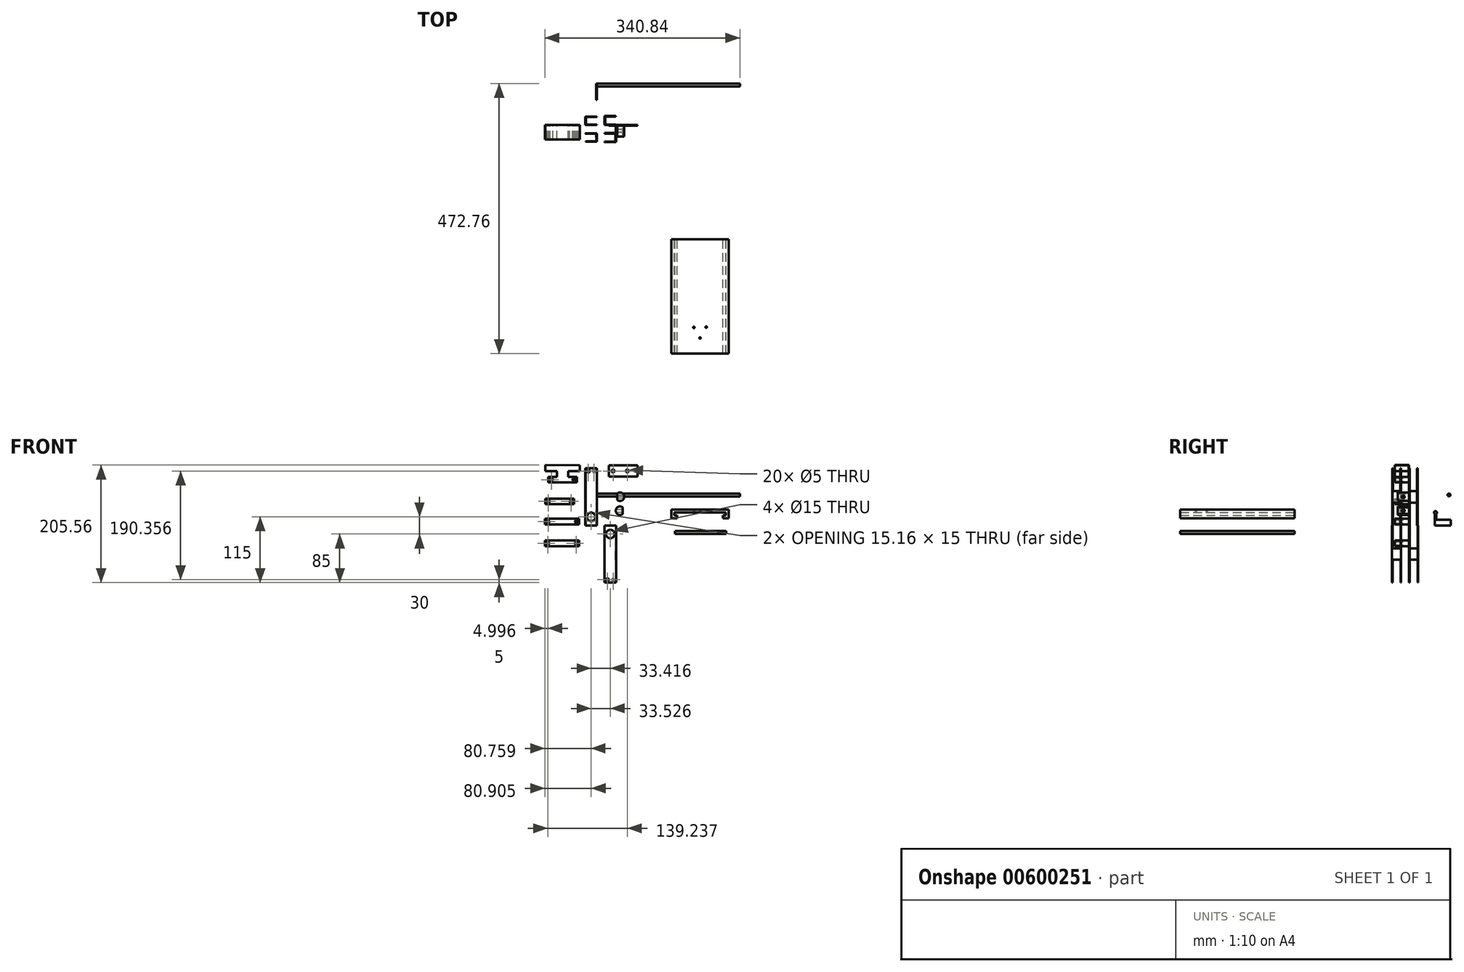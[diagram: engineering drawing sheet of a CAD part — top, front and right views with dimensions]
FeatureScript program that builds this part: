
annotation { "Feature Type Name" : "Feature", "Feature Type Description" : "" }
export const myFeature = defineFeature(function(context is Context, id is Id, definition is map)
    precondition{}
    {
        {
            var Q0;
            Q0=qCreatedBy(makeId("Top.planeOp"),FACE);
            var sketch = newSketch(context, id + "F0", { "sketchPlane" : qUnion([Q0])});
            skLineSegment(sketch, "E0", {"start": v(0, 15) * mm, "end": v(-20, 15) * mm});
            skLineSegment(sketch, "E1", {"start": v(-20, 15) * mm, "end": v(-20, 0) * mm});
            skLineSegment(sketch, "E2", {"start": v(-20, 0) * mm, "end": v(0, 0) * mm});
            skLineSegment(sketch, "E3", {"start": v(0, 0) * mm, "end": v(0, 1) * mm});
            skLineSegment(sketch, "E4", {"start": v(0, 1) * mm, "end": v(-19, 1) * mm});
            skLineSegment(sketch, "E5", {"start": v(-19, 1) * mm, "end": v(-19, 14) * mm});
            skLineSegment(sketch, "E6", {"start": v(-19, 14) * mm, "end": v(0, 14) * mm});
            skLineSegment(sketch, "E7", {"start": v(0, 14) * mm, "end": v(0, 15) * mm});
            skLineSegment(sketch, "E8", {"start": v(33.42, 1) * mm, "end": v(14.42, 1) * mm});
            skLineSegment(sketch, "E9", {"start": v(14.42, 1) * mm, "end": v(14.42, 15) * mm});
            skLineSegment(sketch, "E10", {"start": v(14.42, 15) * mm, "end": v(33.42, 15) * mm});
            skLineSegment(sketch, "E11", {"start": v(33.42, 15) * mm, "end": v(33.42, 16) * mm});
            skLineSegment(sketch, "E12", {"start": v(33.42, 16) * mm, "end": v(13.42, 16) * mm});
            skLineSegment(sketch, "E13", {"start": v(13.42, 16) * mm, "end": v(13.42, 0) * mm});
            skLineSegment(sketch, "E14", {"start": v(13.42, 0) * mm, "end": v(33.42, 0) * mm});
            skLineSegment(sketch, "E15", {"start": v(33.42, 0) * mm, "end": v(33.42, 1) * mm});
            skLineSegment(sketch, "E16", {"start": v(-36.62, -7.13) * mm, "end": v(38.64, -6.85) * mm, "construction": true});
            skLineSegment(sketch, "E17.MirrorCS", {"start": v(-19, 16) * mm, "end": v(0, 16) * mm});
            skLineSegment(sketch, "E18.MirrorCS", {"start": v(-19.95, -14.13) * mm, "end": v(0.05, -13.99) * mm});
            skLineSegment(sketch, "E19.MirrorCS", {"start": v(0.16, -28.99) * mm, "end": v(-19.84, -29.13) * mm});
            skLineSegment(sketch, "E20.MirrorCS", {"start": v(13.47, -13.89) * mm, "end": v(33.47, -13.74) * mm});
            skLineSegment(sketch, "E21.MirrorCS", {"start": v(33.58, -29.74) * mm, "end": v(13.58, -29.89) * mm});
            skLineSegment(sketch, "E22", {"start": v(13.47, -13.89) * mm, "end": v(13.47, -14.89) * mm});
            skLineSegment(sketch, "E23", {"start": v(13.47, -14.89) * mm, "end": v(32.47, -14.75) * mm});
            skLineSegment(sketch, "E24", {"start": v(32.58, -28.75) * mm, "end": v(13.58, -28.89) * mm});
            skLineSegment(sketch, "E25", {"start": v(13.58, -28.89) * mm, "end": v(13.58, -29.89) * mm});
            skLineSegment(sketch, "E26", {"start": v(32.58, -28.75) * mm, "end": v(32.47, -14.75) * mm});
            skLineSegment(sketch, "E27", {"start": v(33.47, -13.74) * mm, "end": v(33.58, -29.74) * mm});
            skLineSegment(sketch, "E28", {"start": v(0.05, -13.99) * mm, "end": v(0.16, -28.99) * mm});
            skLineSegment(sketch, "E29", {"start": v(-19.95, -14.13) * mm, "end": v(-19.94, -15.13) * mm});
            skLineSegment(sketch, "E30", {"start": v(-19.94, -15.13) * mm, "end": v(-0.94, -15) * mm});
            skLineSegment(sketch, "E31", {"start": v(-0.94, -15) * mm, "end": v(-0.85, -28) * mm});
            skLineSegment(sketch, "E32", {"start": v(-0.85, -28) * mm, "end": v(-19.84, -28.13) * mm});
            skLineSegment(sketch, "E33", {"start": v(-19.84, -29.13) * mm, "end": v(-19.84, -28.13) * mm});
            skSolve(sketch);
        }
        {
            var Q0;
            Q0=makeQuery(id+"F0.imprint","IMPRINT",FACE,{"disambiguationData":[TD([[makeQuery(id+"F0.imprint","IMPRINT",EDGE,{"derivedFrom":sQuery(id+"F0.wireOp",EDGE,"E0")}),1.0]])]});
            var Q1;
            Q1=makeQuery(id+"F0.imprint","IMPRINT",FACE,{"disambiguationData":[TD([[makeQuery(id+"F0.imprint","IMPRINT",EDGE,{"derivedFrom":sQuery(id+"F0.wireOp",EDGE,"E19.MirrorCS")}),-1.0]])]});
            extrude(context, id + "F1", {"entities" : qUnion([Q0, Q1]), "depth" : 100 * mm, "offsetDistance" : 25 * mm});
        }
        {
            var Q0;
            Q0=makeQuery(id+"F1.opExtrude","SWEPT_FACE",FACE,{"disambiguationData":[OSD([sQuery(id+"F0.wireOp",EDGE,"E2")])]});
            var sketch = newSketch(context, id + "F2", { "sketchPlane" : qUnion([Q0])});
            skCircle(sketch, "E34", {"center": v(-10, 15) * mm, "radius": 7.5 * mm});
            skPoint(sketch, "E34.centerSnap0", {"position": v(-10, 0) * mm});
            skCircle(sketch, "E35", {"center": v(-5, 95) * mm, "radius": 2.5 * mm});
            skSolve(sketch);
        }
        {
            var Q0;
            Q0=makeQuery(id+"F2.imprint","IMPRINT",FACE,{"disambiguationData":[TD([[makeQuery(id+"F2.imprint","IMPRINT",EDGE,{"derivedFrom":sQuery(id+"F2.wireOp",EDGE,"E34")}),1.0]])]});
            var Q1;
            Q1=makeQuery(id+"F2.imprint","IMPRINT",FACE,{"disambiguationData":[TD([[makeQuery(id+"F2.imprint","IMPRINT",EDGE,{"derivedFrom":sQuery(id+"F2.wireOp",EDGE,"E35")}),1.0]])]});
            extrude(context, id + "F3", {"entities" : qUnion([Q0, Q1]), "operationType" : NewBodyOperationType.REMOVE, "endBound" : BoundingType.THROUGH_ALL, "oppositeDirection" : true, "depth" : 25 * mm, "offsetDistance" : 25 * mm});
        }
        {
            var Q0;
            Q0=makeQuery(id+"F1.opExtrude","SWEPT_FACE",FACE,{"disambiguationData":[OSD([sQuery(id+"F0.wireOp",EDGE,"E1")])]});
            var sketch = newSketch(context, id + "F4", { "sketchPlane" : qUnion([Q0])});
            skPoint(sketch, "E36.centerSnap0", {"position": v(-7.5, 0) * mm});
            skLineSegment(sketch, "E37", {"start": v(-14, 0) * mm, "end": v(-14, 40) * mm});
            skLineSegment(sketch, "E38", {"start": v(-14, 40) * mm, "end": v(-1, 40) * mm});
            skLineSegment(sketch, "E39", {"start": v(-1, 40) * mm, "end": v(-1, 0) * mm});
            skLineSegment(sketch, "E40", {"start": v(-14, 100) * mm, "end": v(-14, 60) * mm});
            skLineSegment(sketch, "E41", {"start": v(-14, 60) * mm, "end": v(-1, 60) * mm});
            skLineSegment(sketch, "E42", {"start": v(-1, 60) * mm, "end": v(-1, 100) * mm});
            skSolve(sketch);
        }
        {
            var Q0;
            {var subQ0=sQuery(id+"F4.wireOp",EDGE,"E37");Q0=makeQuery(id+"F4.imprint","IMPRINT",FACE,{"disambiguationData":[TD([[makeQuery(id+"F4.imprint","IMPRINT",EDGE,{"derivedFrom":subQ0}),-1.0]])]});}
            var Q1;
            {var subQ0=sQuery(id+"F4.wireOp",EDGE,"E40");Q1=makeQuery(id+"F4.imprint","IMPRINT",FACE,{"disambiguationData":[TD([[makeQuery(id+"F4.imprint","IMPRINT",EDGE,{"derivedFrom":subQ0}),1.0]])]});}
            extrude(context, id + "F5", {"entities" : qUnion([Q0, Q1]), "operationType" : NewBodyOperationType.REMOVE, "endBound" : BoundingType.THROUGH_ALL, "oppositeDirection" : true, "depth" : 25 * mm, "offsetDistance" : 25 * mm});
        }
        {
            var Q0;
            Q0=makeQuery(id+"F0.imprint","IMPRINT",FACE,{"disambiguationData":[TD([[makeQuery(id+"F0.imprint","IMPRINT",EDGE,{"derivedFrom":sQuery(id+"F0.wireOp",EDGE,"E8")}),1.0]])]});
            var Q1;
            Q1=makeQuery(id+"F0.imprint","IMPRINT",FACE,{"disambiguationData":[TD([[makeQuery(id+"F0.imprint","IMPRINT",EDGE,{"derivedFrom":sQuery(id+"F0.wireOp",EDGE,"E20.MirrorCS")}),-1.0]])]});
            extrude(context, id + "F6", {"entities" : qUnion([Q0, Q1]), "oppositeDirection" : true, "depth" : 100 * mm, "offsetDistance" : 25 * mm});
        }
        {
            var Q0;
            Q0=makeQuery(id+"F6.opExtrude","SWEPT_FACE",FACE,{"disambiguationData":[OSD([sQuery(id+"F0.wireOp",EDGE,"E14")])]});
            var sketch = newSketch(context, id + "F7", { "sketchPlane" : qUnion([Q0])});
            skCircle(sketch, "E43", {"center": v(23.42, -15) * mm, "radius": 7.5 * mm});
            skPoint(sketch, "E43.centerSnap0", {"position": v(23.42, 0) * mm});
            skCircle(sketch, "E44", {"center": v(28.42, -95) * mm, "radius": 2.5 * mm});
            skSolve(sketch);
        }
        {
            var Q0;
            Q0=makeQuery(id+"F7.imprint","IMPRINT",FACE,{"disambiguationData":[TD([[makeQuery(id+"F7.imprint","IMPRINT",EDGE,{"derivedFrom":sQuery(id+"F7.wireOp",EDGE,"E43")}),1.0]])]});
            var Q1;
            Q1=makeQuery(id+"F7.imprint","IMPRINT",FACE,{"disambiguationData":[TD([[makeQuery(id+"F7.imprint","IMPRINT",EDGE,{"derivedFrom":sQuery(id+"F7.wireOp",EDGE,"E44")}),1.0]])]});
            extrude(context, id + "F8", {"entities" : qUnion([Q0, Q1]), "operationType" : NewBodyOperationType.REMOVE, "endBound" : BoundingType.THROUGH_ALL, "oppositeDirection" : true, "depth" : 25 * mm, "offsetDistance" : 25 * mm});
        }
        {
            var Q0;
            Q0=makeQuery(id+"F6.opExtrude","SWEPT_FACE",FACE,{"disambiguationData":[OSD([sQuery(id+"F0.wireOp",EDGE,"E13")])]});
            var sketch = newSketch(context, id + "F9", { "sketchPlane" : qUnion([Q0])});
            skLineSegment(sketch, "E45", {"start": v(-15, 0) * mm, "end": v(-15, -40) * mm});
            skLineSegment(sketch, "E46", {"start": v(-15, -40) * mm, "end": v(-1, -40) * mm});
            skLineSegment(sketch, "E47", {"start": v(-1, -40) * mm, "end": v(-1, 0) * mm});
            skLineSegment(sketch, "E48", {"start": v(-15, -100) * mm, "end": v(-15, -60) * mm});
            skLineSegment(sketch, "E49", {"start": v(-15, -60) * mm, "end": v(-1, -60) * mm});
            skLineSegment(sketch, "E50", {"start": v(-1, -60) * mm, "end": v(-1, -100) * mm});
            skSolve(sketch);
        }
        {
            var Q0;
            {var subQ0=sQuery(id+"F9.wireOp",EDGE,"E45");Q0=makeQuery(id+"F9.imprint","IMPRINT",FACE,{"disambiguationData":[TD([[makeQuery(id+"F9.imprint","IMPRINT",EDGE,{"derivedFrom":subQ0}),1.0]])]});}
            var Q1;
            {var subQ0=sQuery(id+"F9.wireOp",EDGE,"E48");Q1=makeQuery(id+"F9.imprint","IMPRINT",FACE,{"disambiguationData":[TD([[makeQuery(id+"F9.imprint","IMPRINT",EDGE,{"derivedFrom":subQ0}),-1.0]])]});}
            extrude(context, id + "F10", {"entities" : qUnion([Q0, Q1]), "operationType" : NewBodyOperationType.REMOVE, "endBound" : BoundingType.THROUGH_ALL, "oppositeDirection" : true, "depth" : 25 * mm, "offsetDistance" : 25 * mm});
        }
        {
            var Q0;
            Q0=qCreatedBy(makeId("Front.planeOp"),FACE);
            var sketch = newSketch(context, id + "F11", { "sketchPlane" : qUnion([Q0])});
            skLineSegment(sketch, "E51.bottom", {"start": v(20.9, 105.36) * mm, "end": v(70.9, 105.36) * mm});
            skLineSegment(sketch, "E51.top", {"start": v(20.9, 85.36) * mm, "end": v(70.9, 85.36) * mm});
            skLineSegment(sketch, "E51.left", {"start": v(20.9, 105.36) * mm, "end": v(20.9, 85.36) * mm});
            skLineSegment(sketch, "E51.right", {"start": v(70.9, 105.36) * mm, "end": v(70.9, 85.36) * mm});
            skCircle(sketch, "E52", {"center": v(28.4, 95.36) * mm, "radius": 2.5 * mm});
            skPoint(sketch, "E52.centerSnap0", {"position": v(20.9, 95.36) * mm});
            skCircle(sketch, "E53.MirrorC", {"center": v(53.4, 95.36) * mm, "radius": 2.5 * mm});
            skSolve(sketch);
        }
        {
            var Q0;
            Q0=makeQuery(id+"F11.imprint","IMPRINT",FACE,{"disambiguationData":[TD([[makeQuery(id+"F11.imprint","IMPRINT",EDGE,{"derivedFrom":sQuery(id+"F11.wireOp",EDGE,"E51.bottom")}),-1.0]])]});
            extrude(context, id + "F12", {"entities" : qUnion([Q0]), "depth" : 1 * mm, "offsetDistance" : 25 * mm});
        }
        {
            var Q0;
            Q0=makeQuery(id+"F1.opExtrude","SWEPT_FACE",FACE,{"disambiguationData":[OSD([sQuery(id+"F0.wireOp",EDGE,"E19.MirrorCS")])]});
            var sketch = newSketch(context, id + "F13", { "sketchPlane" : qUnion([Q0])});
            skCircle(sketch, "E54", {"center": v(-15.05, 95) * mm, "radius": 2.5 * mm});
            skCircle(sketch, "E55", {"center": v(-10.05, 15) * mm, "radius": 7.5 * mm});
            skPoint(sketch, "E55.centerSnap0", {"position": v(-10.05, 0) * mm});
            skSolve(sketch);
        }
        {
            var Q0;
            Q0=makeQuery(id+"F13.imprint","IMPRINT",FACE,{"disambiguationData":[TD([[makeQuery(id+"F13.imprint","IMPRINT",EDGE,{"derivedFrom":sQuery(id+"F13.wireOp",EDGE,"E54")}),1.0]])]});
            var Q1;
            Q1=makeQuery(id+"F13.imprint","IMPRINT",FACE,{"disambiguationData":[TD([[makeQuery(id+"F13.imprint","IMPRINT",EDGE,{"derivedFrom":sQuery(id+"F13.wireOp",EDGE,"E55")}),1.0]])]});
            extrude(context, id + "F14", {"entities" : qUnion([Q0, Q1]), "operationType" : NewBodyOperationType.REMOVE, "endBound" : BoundingType.THROUGH_ALL, "oppositeDirection" : true, "depth" : 25 * mm, "offsetDistance" : 25 * mm});
        }
        {
            var Q0;
            Q0=makeQuery(id+"F6.opExtrude","SWEPT_FACE",FACE,{"disambiguationData":[OSD([sQuery(id+"F0.wireOp",EDGE,"E21.MirrorCS")])]});
            var sketch = newSketch(context, id + "F15", { "sketchPlane" : qUnion([Q0])});
            skCircle(sketch, "E56", {"center": v(23.36, -15) * mm, "radius": 7.5 * mm});
            skPoint(sketch, "E56.centerSnap0", {"position": v(23.36, 0) * mm});
            skCircle(sketch, "E57", {"center": v(18.36, -95) * mm, "radius": 2.5 * mm});
            skSolve(sketch);
        }
        {
            var Q0;
            Q0=qSketchRegion(id+"F15",true);
            extrude(context, id + "F16", {"entities" : qUnion([Q0]), "operationType" : NewBodyOperationType.REMOVE, "endBound" : BoundingType.THROUGH_ALL, "oppositeDirection" : true, "depth" : 25 * mm, "offsetDistance" : 25 * mm});
        }
        {
            var Q0;
            Q0=makeQuery(id+"F6.opExtrude","SWEPT_FACE",FACE,{"disambiguationData":[OSD([sQuery(id+"F0.wireOp",EDGE,"E27")])]});
            var sketch = newSketch(context, id + "F17", { "sketchPlane" : qUnion([Q0])});
            skLineSegment(sketch, "E58", {"start": v(-14.99, -40) * mm, "end": v(-28.99, -40) * mm});
            skLineSegment(sketch, "E59", {"start": v(-28.99, -40) * mm, "end": v(-28.99, 0) * mm});
            skLineSegment(sketch, "E60", {"start": v(-14.99, -40) * mm, "end": v(-14.99, 0) * mm});
            skLineSegment(sketch, "E61", {"start": v(-28.99, -100) * mm, "end": v(-28.99, -60) * mm});
            skLineSegment(sketch, "E62", {"start": v(-28.99, -60) * mm, "end": v(-14.99, -60) * mm});
            skLineSegment(sketch, "E63", {"start": v(-14.99, -60) * mm, "end": v(-14.99, -100) * mm});
            skSolve(sketch);
        }
        {
            var Q0;
            Q0=makeQuery(id+"F17.imprint","IMPRINT",FACE,{"disambiguationData":[TD([[makeQuery(id+"F17.imprint","IMPRINT",EDGE,{"derivedFrom":sQuery(id+"F17.wireOp",EDGE,"E58")}),-1.0]])]});
            var Q1;
            {var subQ0=sQuery(id+"F17.wireOp",EDGE,"E61");Q1=makeQuery(id+"F17.imprint","IMPRINT",FACE,{"disambiguationData":[TD([[makeQuery(id+"F17.imprint","IMPRINT",EDGE,{"derivedFrom":subQ0}),-1.0]])]});}
            extrude(context, id + "F18", {"entities" : qUnion([Q0, Q1]), "operationType" : NewBodyOperationType.REMOVE, "endBound" : BoundingType.THROUGH_ALL, "oppositeDirection" : true, "depth" : 25 * mm, "offsetDistance" : 25 * mm});
        }
        {
            var Q0;
            Q0=makeQuery(id+"F1.opExtrude","SWEPT_FACE",FACE,{"disambiguationData":[OSD([sQuery(id+"F0.wireOp",EDGE,"E28")])]});
            var sketch = newSketch(context, id + "F19", { "sketchPlane" : qUnion([Q0])});
            skLineSegment(sketch, "E64", {"start": v(-14.99, 0) * mm, "end": v(-14.99, 40) * mm});
            skLineSegment(sketch, "E65", {"start": v(-14.99, 40) * mm, "end": v(-27.99, 40) * mm});
            skLineSegment(sketch, "E66", {"start": v(-27.99, 40) * mm, "end": v(-27.99, 0) * mm});
            skLineSegment(sketch, "E67", {"start": v(-27.99, 100) * mm, "end": v(-27.99, 60) * mm});
            skLineSegment(sketch, "E68", {"start": v(-27.99, 60) * mm, "end": v(-14.99, 60) * mm});
            skLineSegment(sketch, "E69", {"start": v(-14.99, 60) * mm, "end": v(-14.99, 100) * mm});
            skSolve(sketch);
        }
        {
            var Q0;
            {var subQ0=sQuery(id+"F19.wireOp",EDGE,"E64");Q0=makeQuery(id+"F19.imprint","IMPRINT",FACE,{"disambiguationData":[TD([[makeQuery(id+"F19.imprint","IMPRINT",EDGE,{"derivedFrom":subQ0}),1.0]])]});}
            var Q1;
            {var subQ0=sQuery(id+"F19.wireOp",EDGE,"E67");Q1=makeQuery(id+"F19.imprint","IMPRINT",FACE,{"disambiguationData":[TD([[makeQuery(id+"F19.imprint","IMPRINT",EDGE,{"derivedFrom":subQ0}),1.0]])]});}
            extrude(context, id + "F20", {"entities" : qUnion([Q0, Q1]), "operationType" : NewBodyOperationType.REMOVE, "oppositeDirection" : true, "depth" : 25 * mm, "offsetDistance" : 25 * mm});
        }
        {
            var Q0;
            Q0=qCreatedBy(makeId("Front.planeOp"),FACE);
            var sketch = newSketch(context, id + "F21", { "sketchPlane" : qUnion([Q0])});
            skArc(sketch, "E70", {"start": v(35.49, 44.6) * mm, "mid": v(47.93, 50.24) * mm, "end": v(35.49, 55.88) * mm});
            skArc(sketch, "E71", {"start": v(45.38, 31.4) * mm, "mid": v(32.93, 25.77) * mm, "end": v(45.38, 20.13) * mm});
            skLineSegment(sketch, "E72", {"start": v(35.49, 55.88) * mm, "end": v(35.49, 44.6) * mm});
            skLineSegment(sketch, "E73.trimOffspring", {"start": v(45.38, 31.4) * mm, "end": v(45.38, 20.13) * mm});
            skPoint(sketch, "E74.orphan", {"position": v(40.43, 57.74) * mm});
            skSolve(sketch);
        }
        {
            var Q0;
            Q0=makeQuery(id+"F21.imprint","IMPRINT",FACE,{"disambiguationData":[TD([[makeQuery(id+"F21.imprint","IMPRINT",EDGE,{"derivedFrom":sQuery(id+"F21.wireOp",EDGE,"E70")}),1.0]])]});
            var Q1;
            Q1=makeQuery(id+"F21.imprint","IMPRINT",FACE,{"disambiguationData":[TD([[makeQuery(id+"F21.imprint","IMPRINT",EDGE,{"derivedFrom":sQuery(id+"F21.wireOp",EDGE,"E71")}),1.0]])]});
            extrude(context, id + "F22", {"entities" : qUnion([Q0, Q1]), "depth" : 20 * mm, "offsetDistance" : 25 * mm});
        }
        {
            var Q0;
            Q0=qCreatedBy(makeId("Right.planeOp"),FACE);
            var sketch = newSketch(context, id + "F23", { "sketchPlane" : qUnion([Q0])});
            skCircle(sketch, "E75", {"center": v(69.88, 53.43) * mm, "radius": 2.5 * mm});
            skSolve(sketch);
        }
        {
            var Q0;
            Q0=makeQuery(id+"F23.imprint","IMPRINT",FACE,{"disambiguationData":[TD([[makeQuery(id+"F23.imprint","IMPRINT",EDGE,{"derivedFrom":sQuery(id+"F23.wireOp",EDGE,"E75")}),1.0]])]});
            extrude(context, id + "F24", {"entities" : qUnion([Q0]), "depth" : 250 * mm, "offsetDistance" : 25 * mm});
        }
        {
            var Q0;
            Q0=qCreatedBy(makeId("Front.planeOp"),FACE);
            var sketch = newSketch(context, id + "F25", { "sketchPlane" : qUnion([Q0])});
            skLineSegment(sketch, "E76.top", {"start": v(-84.95, 75.12) * mm, "end": v(-34.95, 75.12) * mm});
            skLineSegment(sketch, "E76.left", {"start": v(-84.95, 85.12) * mm, "end": v(-84.95, 75.12) * mm});
            skLineSegment(sketch, "E76.right", {"start": v(-34.95, 85.12) * mm, "end": v(-34.95, 75.12) * mm});
            skCircle(sketch, "E77", {"center": v(-79.38, 80.12) * mm, "radius": 2.5 * mm});
            skPoint(sketch, "E77.centerSnap0", {"position": v(-84.95, 80.12) * mm});
            skCircle(sketch, "E78", {"center": v(-39.95, 80.12) * mm, "radius": 2.41 * mm});
            skPoint(sketch, "E78.centerSnap0", {"position": v(-34.95, 80.12) * mm});
            skLineSegment(sketch, "E79.MirrorCS", {"start": v(-89.95, 47.06) * mm, "end": v(-39.95, 47.06) * mm});
            skLineSegment(sketch, "E80.MirrorCS", {"start": v(-89.95, 37.06) * mm, "end": v(-89.95, 47.06) * mm});
            skLineSegment(sketch, "E81.MirrorCS", {"start": v(-89.95, 37.06) * mm, "end": v(-39.95, 37.06) * mm});
            skLineSegment(sketch, "E82.MirrorCS", {"start": v(-39.95, 37.06) * mm, "end": v(-39.95, 47.06) * mm});
            skCircle(sketch, "E83", {"center": v(-84.95, 42.06) * mm, "radius": 2.5 * mm});
            skPoint(sketch, "E83.centerSnap0", {"position": v(-89.95, 42.06) * mm});
            skCircle(sketch, "E84", {"center": v(-44.95, 42.06) * mm, "radius": 2.5 * mm});
            skPoint(sketch, "E84.centerSnap0", {"position": v(-39.95, 42.06) * mm});
            skLineSegment(sketch, "E85.bottom", {"start": v(-90.84, 11.74) * mm, "end": v(-30.84, 11.74) * mm});
            skLineSegment(sketch, "E85.top", {"start": v(-90.84, 1.74) * mm, "end": v(-30.84, 1.74) * mm});
            skLineSegment(sketch, "E85.left", {"start": v(-90.84, 11.74) * mm, "end": v(-90.84, 1.74) * mm});
            skLineSegment(sketch, "E85.right", {"start": v(-30.84, 11.74) * mm, "end": v(-30.84, 1.74) * mm});
            skCircle(sketch, "E86", {"center": v(-85.27, 6.74) * mm, "radius": 2.5 * mm});
            skPoint(sketch, "E86.centerSnap0", {"position": v(-90.84, 6.74) * mm});
            skCircle(sketch, "E87", {"center": v(-35.84, 6.74) * mm, "radius": 2.41 * mm});
            skPoint(sketch, "E87.centerSnap0", {"position": v(-30.84, 6.74) * mm});
            skLineSegment(sketch, "E88.MirrorCS", {"start": v(-90.84, -36.32) * mm, "end": v(-90.84, -26.32) * mm});
            skLineSegment(sketch, "E89.MirrorCS", {"start": v(-30.84, -36.32) * mm, "end": v(-30.84, -26.32) * mm});
            skCircle(sketch, "E90", {"center": v(-85.84, -31.32) * mm, "radius": 2.5 * mm});
            skPoint(sketch, "E90.centerSnap0", {"position": v(-90.84, -31.32) * mm});
            skCircle(sketch, "E91", {"center": v(-35.84, -31.32) * mm, "radius": 2.5 * mm});
            skPoint(sketch, "E91.centerSnap0", {"position": v(-30.84, -31.32) * mm});
            skLineSegment(sketch, "E92", {"start": v(-90.84, -26.32) * mm, "end": v(-30.84, -26.32) * mm});
            skLineSegment(sketch, "E93", {"start": v(-90.84, -36.32) * mm, "end": v(-30.84, -36.32) * mm});
            skLineSegment(sketch, "E94", {"start": v(-69.95, 85.12) * mm, "end": v(-69.95, 95.12) * mm});
            skLineSegment(sketch, "E95.MirrorCS", {"start": v(-49.95, 85.12) * mm, "end": v(-49.95, 95.12) * mm});
            skLineSegment(sketch, "E96.MirrorCS", {"start": v(-89.95, 135.12) * mm, "end": v(-39.95, 135.12) * mm});
            skLineSegment(sketch, "E97.MirrorCS", {"start": v(-84.95, 85.12) * mm, "end": v(-69.95, 85.12) * mm});
            skLineSegment(sketch, "E98", {"start": v(-89.95, 95.12) * mm, "end": v(-89.95, 105.56) * mm});
            skLineSegment(sketch, "E99", {"start": v(-29.95, 105.12) * mm, "end": v(-29.95, 95.12) * mm});
            skLineSegment(sketch, "E100.trimOffspring", {"start": v(-49.95, 95.12) * mm, "end": v(-29.95, 95.12) * mm});
            skLineSegment(sketch, "E101", {"start": v(-69.95, 95.12) * mm, "end": v(-89.95, 95.12) * mm});
            skLineSegment(sketch, "E102.trimOffspring", {"start": v(-49.95, 85.12) * mm, "end": v(-34.95, 85.12) * mm});
            skPoint(sketch, "E103.end.orphan", {"position": v(-59.95, 75.12) * mm});
            skPoint(sketch, "E103.start.orphan", {"position": v(-59.95, 85.12) * mm});
            skLineSegment(sketch, "E104", {"start": v(-29.95, 105.12) * mm, "end": v(-89.95, 105.56) * mm});
            skLineSegment(sketch, "E105", {"start": v(-59.95, 75.12) * mm, "end": v(-59.95, 105.34) * mm, "construction": true});
            skSolve(sketch);
        }
        {
            var Q0;
            Q0=makeQuery(id+"F25.imprint","IMPRINT",FACE,{"disambiguationData":[TD([[makeQuery(id+"F25.imprint","IMPRINT",EDGE,{"derivedFrom":sQuery(id+"F25.wireOp",EDGE,"E76.bottom")}),-1.0]])]});
            var Q1;
            {var subQ2=sQuery(id+"F25.wireOp",EDGE,"E80.MirrorCS");Q1=makeQuery(id+"F25.imprint","IMPRINT",FACE,{"disambiguationData":[TD([[makeQuery(id+"F25.imprint","IMPRINT",EDGE,{"derivedFrom":subQ2}),-1.0]])]});}
            var Q2;
            Q2=makeQuery(id+"F25.imprint","IMPRINT",FACE,{"disambiguationData":[TD([[makeQuery(id+"F25.imprint","IMPRINT",EDGE,{"derivedFrom":sQuery(id+"F25.wireOp",EDGE,"E76.top")}),1.0]])]});
            extrude(context, id + "F26", {"entities" : qUnion([Q0, Q1, Q2]), "depth" : 25 * mm, "offsetDistance" : 25 * mm});
        }
        {
            var Q0;
            Q0=makeQuery(id+"F25.imprint","IMPRINT",FACE,{"disambiguationData":[TD([[makeQuery(id+"F25.imprint","IMPRINT",EDGE,{"derivedFrom":sQuery(id+"F25.wireOp",EDGE,"E88.MirrorCS")}),-1.0]])]});
            var Q1;
            Q1=makeQuery(id+"F25.imprint","IMPRINT",FACE,{"disambiguationData":[TD([[makeQuery(id+"F25.imprint","IMPRINT",EDGE,{"derivedFrom":sQuery(id+"F25.wireOp",EDGE,"E85.bottom")}),-1.0]])]});
            extrude(context, id + "F27", {"entities" : qUnion([Q0, Q1]), "depth" : 25 * mm, "offsetDistance" : 25 * mm});
        }
        {
            var Q0;
            Q0=makeQuery(id+"F22.opExtrude","SWEPT_FACE",FACE,{"disambiguationData":[OSD([sQuery(id+"F21.wireOp",EDGE,"E73.trimOffspring")])]});
            var sketch = newSketch(context, id + "F28", { "sketchPlane" : qUnion([Q0])});
            skCircle(sketch, "E106", {"center": v(-10, 25.77) * mm, "radius": 2.5 * mm});
            skPoint(sketch, "E106.centerSnap0", {"position": v(-20, 25.77) * mm});
            skPoint(sketch, "E106.centerSnap1", {"position": v(-10, 31.4) * mm});
            skSolve(sketch);
        }
        {
            var Q0;
            Q0=makeQuery(id+"F28.imprint","IMPRINT",FACE,{"disambiguationData":[TD([[makeQuery(id+"F28.imprint","IMPRINT",EDGE,{"derivedFrom":sQuery(id+"F28.wireOp",EDGE,"E106")}),1.0]])]});
            extrude(context, id + "F29", {"entities" : qUnion([Q0]), "operationType" : NewBodyOperationType.REMOVE, "endBound" : BoundingType.THROUGH_ALL, "oppositeDirection" : true, "depth" : 25 * mm, "offsetDistance" : 25 * mm});
        }
        {
            var Q0;
            Q0=makeQuery(id+"F22.opExtrude","SWEPT_FACE",FACE,{"disambiguationData":[OSD([sQuery(id+"F21.wireOp",EDGE,"E72")])]});
            var sketch = newSketch(context, id + "F30", { "sketchPlane" : qUnion([Q0])});
            skCircle(sketch, "E107", {"center": v(10, 50.24) * mm, "radius": 2.5 * mm});
            skPoint(sketch, "E107.centerSnap0", {"position": v(10, 44.6) * mm});
            skPoint(sketch, "E107.centerSnap1", {"position": v(0, 50.24) * mm});
            skSolve(sketch);
        }
        {
            var Q0;
            Q0=makeQuery(id+"F30.imprint","IMPRINT",FACE,{"disambiguationData":[TD([[makeQuery(id+"F30.imprint","IMPRINT",EDGE,{"derivedFrom":sQuery(id+"F30.wireOp",EDGE,"E107")}),1.0]])]});
            extrude(context, id + "F31", {"entities" : qUnion([Q0]), "operationType" : NewBodyOperationType.REMOVE, "endBound" : BoundingType.THROUGH_ALL, "oppositeDirection" : true, "depth" : 25 * mm, "offsetDistance" : 25 * mm});
        }
        {
            var Q0;
            Q0=qCreatedBy(makeId("Right.planeOp"),FACE);
            var sketch = newSketch(context, id + "F32", { "sketchPlane" : qUnion([Q0])});
            skArc(sketch, "E108", {"start": v(47.76, 20.47) * mm, "mid": v(46.3, 25) * mm, "end": v(44.85, 20.47) * mm});
            skLineSegment(sketch, "E109", {"start": v(47.76, 8.68) * mm, "end": v(47.76, 20.47) * mm});
            skLineSegment(sketch, "E110.MirrorCS", {"start": v(44.85, 8.68) * mm, "end": v(44.85, 20.47) * mm});
            skLineSegment(sketch, "E111", {"start": v(37.92, 27.31) * mm, "end": v(57.96, 27.31) * mm, "construction": true});
            skLineSegment(sketch, "E112", {"start": v(44.85, 8.68) * mm, "end": v(44.85, 0) * mm});
            skLineSegment(sketch, "E113", {"start": v(44.85, 0) * mm, "end": v(47.76, 0) * mm});
            skLineSegment(sketch, "E114", {"start": v(47.76, 0) * mm, "end": v(47.76, 8.68) * mm});
            skArc(sketch, "E115.MirrorCS", {"start": v(47.76, 34.16) * mm, "mid": v(46.3, 29.63) * mm, "end": v(44.85, 34.16) * mm});
            skLineSegment(sketch, "E116.MirrorCS", {"start": v(44.85, 45.94) * mm, "end": v(44.85, 34.16) * mm});
            skLineSegment(sketch, "E117.MirrorCS", {"start": v(47.76, 45.94) * mm, "end": v(47.76, 34.16) * mm});
            skLineSegment(sketch, "E118.MirrorCS", {"start": v(44.85, 45.94) * mm, "end": v(44.85, 54.62) * mm});
            skLineSegment(sketch, "E119.MirrorCS", {"start": v(47.76, 54.62) * mm, "end": v(47.76, 45.94) * mm});
            skLineSegment(sketch, "E120.MirrorCS", {"start": v(44.85, 54.62) * mm, "end": v(47.76, 54.62) * mm});
            skSolve(sketch);
        }
        {
            var Q0;
            Q0=makeQuery(id+"F32.imprint","IMPRINT",FACE,{"disambiguationData":[TD([[makeQuery(id+"F32.imprint","IMPRINT",EDGE,{"derivedFrom":sQuery(id+"F32.wireOp",EDGE,"E108")}),1.0]])]});
            var Q1;
            Q1=makeQuery(id+"F32.imprint","IMPRINT",FACE,{"disambiguationData":[TD([[makeQuery(id+"F32.imprint","IMPRINT",EDGE,{"derivedFrom":sQuery(id+"F32.wireOp",EDGE,"E115.MirrorCS")}),-1.0]])]});
            extrude(context, id + "F33", {"entities" : qUnion([Q0, Q1]), "oppositeDirection" : true, "depth" : 1 * mm, "offsetDistance" : 25 * mm});
        }
        {
            var Q0;
            Q0=makeQuery(id+"F33.opExtrude","SWEPT_FACE",FACE,{"disambiguationData":[OSD([sQuery(id+"F32.wireOp",EDGE,"E109"),sQuery(id+"F32.wireOp",EDGE,"E114")])]});
            var sketch = newSketch(context, id + "F34", { "sketchPlane" : qUnion([Q0])});
            skLineSegment(sketch, "E121", {"start": v(0, 10) * mm, "end": v(1, 10) * mm});
            skLineSegment(sketch, "E122", {"start": v(0.98, 44.62) * mm, "end": v(0, 44.62) * mm});
            skSolve(sketch);
        }
        {
            var Q0;
            {var subQ0=sQuery(id+"F34.wireOp",EDGE,"E121");Q0=makeQuery(id+"F34.imprint","IMPRINT",FACE,{"disambiguationData":[TD([[makeQuery(id+"F34.imprint","IMPRINT",EDGE,{"derivedFrom":subQ0}),-1.0]])]});}
            extrude(context, id + "F35", {"entities" : qUnion([Q0]), "operationType" : NewBodyOperationType.ADD, "depth" : 25 * mm, "offsetDistance" : 25 * mm});
        }
        {
            var Q0;
            Q0=qCreatedBy(makeId("Front.planeOp"),FACE);
            var sketch = newSketch(context, id + "F36", { "sketchPlane" : qUnion([Q0])});
            skLineSegment(sketch, "E123", {"start": v(181.33, -15) * mm, "end": v(136.33, -15) * mm});
            skLineSegment(sketch, "E124", {"start": v(136.33, -15) * mm, "end": v(136.33, -10) * mm});
            skLineSegment(sketch, "E125", {"start": v(136.33, -10) * mm, "end": v(181.33, -10) * mm});
            skLineSegment(sketch, "E126", {"start": v(181.33, -10) * mm, "end": v(181.33, -15) * mm, "construction": true});
            skLineSegment(sketch, "E127.MirrorCS", {"start": v(226.33, -10) * mm, "end": v(181.33, -10) * mm});
            skLineSegment(sketch, "E128.MirrorCS", {"start": v(181.33, -15) * mm, "end": v(226.33, -15) * mm});
            skLineSegment(sketch, "E129.MirrorCS", {"start": v(226.33, -15) * mm, "end": v(226.33, -10) * mm});
            skLineSegment(sketch, "E130", {"start": v(119.38, 8.74) * mm, "end": v(249.77, 8.74) * mm, "construction": true});
            skLineSegment(sketch, "E131.MirrorCS", {"start": v(243.3, 8.74) * mm, "end": v(112.9, 8.74) * mm, "construction": true});
            skLineSegment(sketch, "E132.MirrorCS", {"start": v(180.38, 22.49) * mm, "end": v(180.38, 27.49) * mm, "construction": true});
            skLineSegment(sketch, "E133.MirrorCS", {"start": v(220.38, 12.49) * mm, "end": v(220.38, 17.49) * mm});
            skLineSegment(sketch, "E134.MirrorCS", {"start": v(135.38, 17.49) * mm, "end": v(140.38, 17.49) * mm});
            skLineSegment(sketch, "E135.MirrorCS", {"start": v(140.38, 12.49) * mm, "end": v(140.38, 17.49) * mm});
            skLineSegment(sketch, "E136.MirrorCS", {"start": v(135.38, 22.49) * mm, "end": v(135.38, 17.49) * mm});
            skLineSegment(sketch, "E137.MirrorCS", {"start": v(225.38, 17.49) * mm, "end": v(220.38, 17.49) * mm});
            skLineSegment(sketch, "E138.MirrorCS", {"start": v(225.38, 22.49) * mm, "end": v(225.38, 17.49) * mm});
            skLineSegment(sketch, "E139.MirrorCS", {"start": v(140.38, 12.49) * mm, "end": v(130.38, 12.49) * mm});
            skLineSegment(sketch, "E140.MirrorCS", {"start": v(220.38, 12.49) * mm, "end": v(230.38, 12.49) * mm});
            skLineSegment(sketch, "E141.MirrorCS", {"start": v(230.38, 27.49) * mm, "end": v(230.38, 12.49) * mm});
            skLineSegment(sketch, "E142.MirrorCS", {"start": v(230.38, 27.49) * mm, "end": v(180.38, 27.49) * mm});
            skLineSegment(sketch, "E143.MirrorCS", {"start": v(135.38, 22.49) * mm, "end": v(180.38, 22.49) * mm});
            skLineSegment(sketch, "E144.MirrorCS", {"start": v(225.38, 22.49) * mm, "end": v(180.38, 22.49) * mm});
            skLineSegment(sketch, "E145.MirrorCS", {"start": v(130.38, 27.49) * mm, "end": v(180.38, 27.49) * mm});
            skLineSegment(sketch, "E146.MirrorCS", {"start": v(130.38, 27.49) * mm, "end": v(130.38, 12.49) * mm});
            skSolve(sketch);
        }
        {
            var Q0;
            Q0=makeQuery(id+"F36.imprint","IMPRINT",FACE,{"disambiguationData":[TD([[makeQuery(id+"F36.imprint","IMPRINT",EDGE,{"derivedFrom":sQuery(id+"F36.wireOp",EDGE,"E135.MirrorCS")}),1.0]])]});
            var Q1;
            Q1=makeQuery(id+"F36.imprint","IMPRINT",FACE,{"disambiguationData":[TD([[makeQuery(id+"F36.imprint","IMPRINT",EDGE,{"derivedFrom":sQuery(id+"F36.wireOp",EDGE,"E124")}),-1.0]])]});
            extrude(context, id + "F37", {"entities" : qUnion([Q0, Q1]), "depth" : 400 * mm, "offsetDistance" : 25 * mm});
        }
        {
            var Q0;
            Q0=makeQuery(id+"F37.opExtrude","SWEPT_FACE",FACE,{"disambiguationData":[OSD([sQuery(id+"F36.wireOp",EDGE,"E143.MirrorCS"),sQuery(id+"F36.wireOp",EDGE,"E144.MirrorCS")])]});
            var sketch = newSketch(context, id + "F38", { "sketchPlane" : qUnion([Q0])});
            skLineSegment(sketch, "E147", {"start": v(135.38, 320) * mm, "end": v(225.38, 320) * mm});
            skCircle(sketch, "E148", {"center": v(180.38, 360) * mm, "radius": 12.5 * mm, "construction": true});
            skPoint(sketch, "E148.centerSnap0", {"position": v(180.38, 400) * mm});
            skCircle(sketch, "E149", {"center": v(180.59, 372.5) * mm, "radius": 1.25 * mm});
            skCircle(sketch, "E150", {"center": v(169.45, 353.93) * mm, "radius": 1.25 * mm});
            skCircle(sketch, "E151", {"center": v(191.1, 353.57) * mm, "radius": 1.25 * mm});
            skLineSegment(sketch, "E152", {"start": v(180.59, 372.5) * mm, "end": v(169.45, 353.93) * mm, "construction": true});
            skLineSegment(sketch, "E153", {"start": v(191.1, 353.57) * mm, "end": v(180.59, 372.5) * mm, "construction": true});
            skLineSegment(sketch, "E154", {"start": v(191.1, 353.57) * mm, "end": v(169.45, 353.93) * mm, "construction": true});
            skSolve(sketch);
        }
        {
            var Q0;
            Q0=makeQuery(id+"F38.imprint","IMPRINT",FACE,{"disambiguationData":[TD([[makeQuery(id+"F38.imprint","IMPRINT",EDGE,{"derivedFrom":sQuery(id+"F38.wireOp",EDGE,"E149")}),1.0]])]});
            var Q1;
            Q1=makeQuery(id+"F38.imprint","IMPRINT",FACE,{"disambiguationData":[TD([[makeQuery(id+"F38.imprint","IMPRINT",EDGE,{"derivedFrom":sQuery(id+"F38.wireOp",EDGE,"E150")}),1.0]])]});
            var Q2;
            Q2=makeQuery(id+"F38.imprint","IMPRINT",FACE,{"disambiguationData":[TD([[makeQuery(id+"F38.imprint","IMPRINT",EDGE,{"derivedFrom":sQuery(id+"F38.wireOp",EDGE,"E151")}),1.0]])]});
            extrude(context, id + "F39", {"entities" : qUnion([Q0, Q1, Q2]), "operationType" : NewBodyOperationType.REMOVE, "endBound" : BoundingType.THROUGH_ALL, "oppositeDirection" : true, "depth" : 1 * mm, "offsetDistance" : 25 * mm});
        }
        {
            var Q0;
            Q0=makeQuery(id+"F37.opExtrude","SWEPT_FACE",FACE,{"disambiguationData":[OSD([sQuery(id+"F36.wireOp",EDGE,"E145.MirrorCS"),sQuery(id+"F36.wireOp",EDGE,"E142.MirrorCS")])]});
            var sketch = newSketch(context, id + "F40", { "sketchPlane" : qUnion([Q0])});
            skLineSegment(sketch, "E155", {"start": v(130.38, -200) * mm, "end": v(230.38, -200) * mm});
            skSolve(sketch);
        }
        {
            var Q0;
            {var subQ0=sQuery(id+"F40.wireOp",EDGE,"E155");Q0=makeQuery(id+"F40.imprint","IMPRINT",FACE,{"disambiguationData":[TD([[makeQuery(id+"F40.imprint","IMPRINT",EDGE,{"derivedFrom":subQ0}),1.0]])]});}
            extrude(context, id + "F41", {"entities" : qUnion([Q0]), "operationType" : NewBodyOperationType.REMOVE, "endBound" : BoundingType.THROUGH_ALL, "oppositeDirection" : true, "depth" : 25 * mm, "offsetDistance" : 25 * mm});
        }
    });
